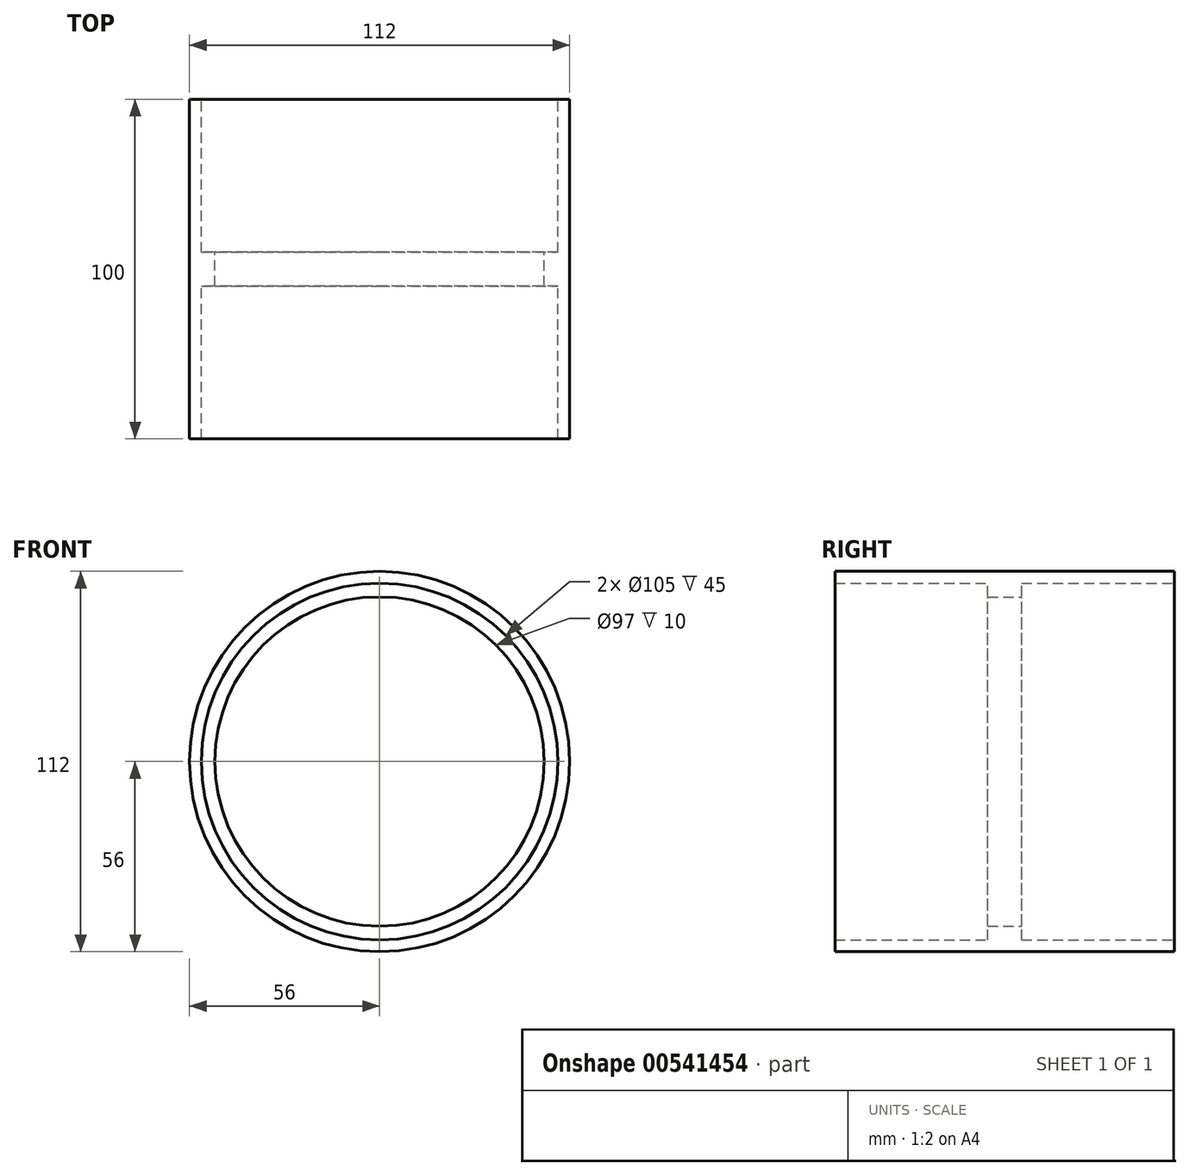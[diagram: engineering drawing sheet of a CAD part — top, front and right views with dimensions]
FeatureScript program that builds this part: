
annotation { "Feature Type Name" : "Feature", "Feature Type Description" : "" }
export const myFeature = defineFeature(function(context is Context, id is Id, definition is map)
    precondition{}
    {
        {
            var Q0;
            Q0=qCreatedBy(makeId("Front.planeOp"),FACE);
            var sketch = newSketch(context, id + "F0", { "sketchPlane" : qUnion([Q0])});
            skCircle(sketch, "E0", {"center": v(0, 0) * mm, "radius": 56 * mm});
            skCircle(sketch, "E1", {"center": v(0, 0) * mm, "radius": 52.5 * mm});
            skSolve(sketch);
        }
        {
            var Q0;
            Q0=makeQuery(id+"F0.imprint","IMPRINT",FACE,{"disambiguationData":[TD([[makeQuery(id+"F0.imprint","IMPRINT",EDGE,{"derivedFrom":sQuery(id+"F0.wireOp",EDGE,"E0")}),1.0]])]});
            extrude(context, id + "F1", {"entities" : qUnion([Q0]), "depth" : 45 * mm, "offsetDistance" : 25 * mm});
        }
        {
            var Q0;
            Q0=makeQuery(id+"F1.opExtrude","CAP_FACE",FACE,{"disambiguationData":[OSD([sQuery(id+"F0.wireOp",EDGE,"E0"),sQuery(id+"F0.wireOp",EDGE,"E1")])],"isStart":false});
            var sketch = newSketch(context, id + "F2", { "sketchPlane" : qUnion([Q0])});
            skCircle(sketch, "E2", {"center": v(0, 0) * mm, "radius": 56 * mm});
            skCircle(sketch, "E3", {"center": v(0, 0) * mm, "radius": 48.5 * mm});
            skSolve(sketch);
        }
        {
            var Q0;
            Q0=makeQuery(id+"F2.imprint","IMPRINT",FACE,{"disambiguationData":[TD([[makeQuery(id+"F2.imprint","IMPRINT",EDGE,{"derivedFrom":sQuery(id+"F2.wireOp",EDGE,"E3")}),-1.0]])]});
            var Q1;
            Q1=makeQuery(id+"F2.imprint","IMPRINT",FACE,{"disambiguationData":[TD([[makeQuery(id+"F2.imprint","IMPRINT",EDGE,{"derivedFrom":sQuery(id+"F2.wireOp",EDGE,"E2")}),1.0]])]});
            extrude(context, id + "F3", {"entities" : qUnion([Q0, Q1]), "operationType" : NewBodyOperationType.ADD, "depth" : 10 * mm, "offsetDistance" : 25 * mm});
        }
        {
            var Q0;
            Q0=makeQuery(id+"F3.opExtrude","CAP_FACE",FACE,{"disambiguationData":[OSD([sQuery(id+"F2.wireOp",EDGE,"E2"),sQuery(id+"F2.wireOp",EDGE,"E3")])],"isStart":false});
            var sketch = newSketch(context, id + "F4", { "sketchPlane" : qUnion([Q0])});
            skCircle(sketch, "E4", {"center": v(0, 0) * mm, "radius": 56 * mm});
            skCircle(sketch, "E5", {"center": v(0, 0) * mm, "radius": 52.5 * mm});
            skSolve(sketch);
        }
        {
            var Q0;
            Q0=makeQuery(id+"F4.imprint","IMPRINT",FACE,{"disambiguationData":[TD([[makeQuery(id+"F4.imprint","IMPRINT",EDGE,{"derivedFrom":sQuery(id+"F4.wireOp",EDGE,"E4")}),1.0]])]});
            extrude(context, id + "F5", {"entities" : qUnion([Q0]), "operationType" : NewBodyOperationType.ADD, "depth" : 45 * mm, "offsetDistance" : 25 * mm});
        }
    });
